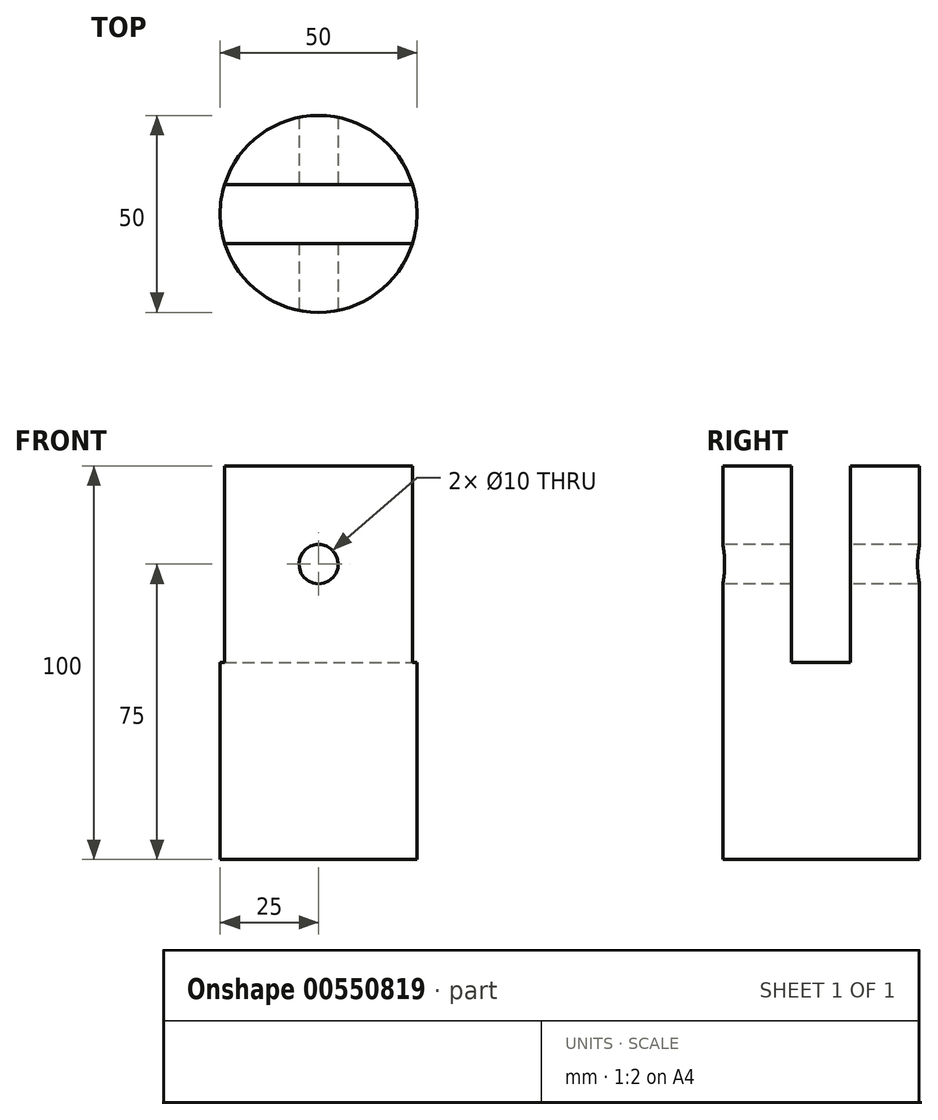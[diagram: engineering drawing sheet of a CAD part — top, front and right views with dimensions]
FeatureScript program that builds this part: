
annotation { "Feature Type Name" : "Feature", "Feature Type Description" : "" }
export const myFeature = defineFeature(function(context is Context, id is Id, definition is map)
    precondition{}
    {
        {
            var Q0;
            Q0=qCreatedBy(makeId("Top.planeOp"),FACE);
            var sketch = newSketch(context, id + "F0", { "sketchPlane" : qUnion([Q0])});
            skCircle(sketch, "E0", {"center": v(0, 0) * mm, "radius": 25 * mm});
            skSolve(sketch);
        }
        {
            var Q0;
            Q0=makeQuery(id+"F0.imprint","IMPRINT",FACE,{"disambiguationData":[TD([[makeQuery(id+"F0.imprint","IMPRINT",EDGE,{"derivedFrom":sQuery(id+"F0.wireOp",EDGE,"E0")}),1.0]])]});
            extrude(context, id + "F1", {"entities" : qUnion([Q0]), "depth" : 50 * mm, "offsetDistance" : 25 * mm});
        }
        {
            var Q0;
            Q0=makeQuery(id+"F1.opExtrude","CAP_FACE",FACE,{"disambiguationData":[OSD([sQuery(id+"F0.wireOp",EDGE,"E0")])],"isStart":false});
            var sketch = newSketch(context, id + "F2", { "sketchPlane" : qUnion([Q0])});
            skArc(sketch, "E1", {"start": v(-23.85, -7.5) * mm, "mid": v(0, -25) * mm, "end": v(23.85, -7.5) * mm});
            skLineSegment(sketch, "E2.bottom", {"start": v(-25, -7.5) * mm, "end": v(25, -7.5) * mm});
            skPoint(sketch, "E2.middle", {"position": v(0, -25) * mm});
            skSolve(sketch);
        }
        {
            var Q0;
            {var subQ0=sQuery(id+"F2.wireOp",EDGE,"E1");Q0=makeQuery(id+"F2.imprint","IMPRINT",FACE,{"disambiguationData":[TD([[makeQuery(id+"F2.imprint","IMPRINT",EDGE,{"derivedFrom":subQ0}),1.0]])]});}
            extrude(context, id + "F3", {"entities" : qUnion([Q0]), "operationType" : NewBodyOperationType.ADD, "depth" : 50 * mm, "offsetDistance" : 25 * mm});
        }
        {
            var Q0;
            Q0=makeQuery(id+"F1.opExtrude","SWEPT_BODY",BODY,{"disambiguationData":[OSD([sQuery(id+"F0.wireOp",EDGE,"E0")])]});
            var Q1;
            Q1=qCreatedBy(makeId("Front.planeOp"),FACE);
            mirror(context, id + "F4", {"operationType" : NewBodyOperationType.ADD, "entities" : qUnion([Q0]), "mirrorPlane" : qUnion([Q1])});
        }
        {
            var Q0;
            Q0=qCreatedBy(makeId("Front.planeOp"),FACE);
            var sketch = newSketch(context, id + "F5", { "sketchPlane" : qUnion([Q0])});
            skCircle(sketch, "E3", {"center": v(0, 75) * mm, "radius": 5 * mm});
            skSolve(sketch);
        }
        {
            var Q0;
            Q0=makeQuery(id+"F5.imprint","IMPRINT",FACE,{"disambiguationData":[TD([[makeQuery(id+"F5.imprint","IMPRINT",EDGE,{"derivedFrom":sQuery(id+"F5.wireOp",EDGE,"E3")}),1.0]])]});
            extrude(context, id + "F6", {"entities" : qUnion([Q0]), "operationType" : NewBodyOperationType.REMOVE, "endBound" : BoundingType.SYMMETRIC, "oppositeDirection" : true, "depth" : 50 * mm, "offsetDistance" : 25 * mm});
        }
    });
